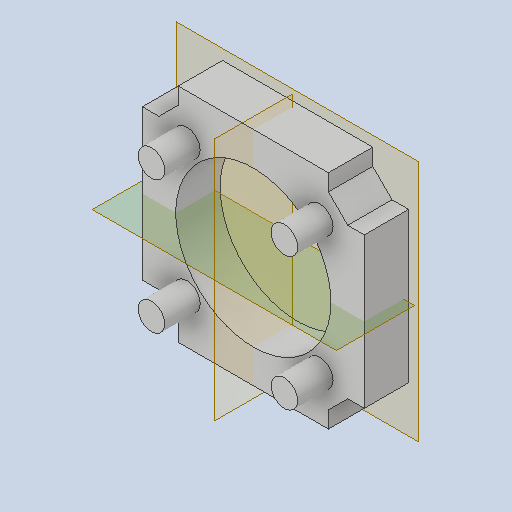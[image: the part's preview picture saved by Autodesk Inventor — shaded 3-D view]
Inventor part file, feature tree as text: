
AUTODESK INVENTOR PART (.ipt)
format: ipt  version: 2023 (Build 270158000, 158)  size: 226,816 bytes
history: native  units: mm
features: reference x19, other x5, plane x4, extrude x4, sketch x4, projected_geometry x1
ambient origin geometry x8: Origin, YZ Plane, XZ Plane, XY Plane, X Axis, Y Axis, Z Axis, Center Point
bodies: Solid1 (feature_tree)
feature tree (37):
  plane  "Work Plane1"
  extrude  "Extrusion1"  Depth=8.0mm TaperAngle=0.0deg
  sketch  "Sketch2"  dims[d18=53.8mm d19=45.0deg]
  plane  "Work Plane2"
  extrude  "Extrusion2"  TaperAngle=45.0deg  [1 undecoded]
  extrude  "Extrusion3"  Depth=45.0mm
  extrude  "Extrusion4"  Depth=10.0mm
  plane  "Arbeitsebene3"
  plane  "Arbeitsebene4"
  sketch  "Sketch1"  dims[d10=10.0mm d11=0.0mm d16=8.0mm d17=0.0mm]
  reference  "Reference1"
  reference  "Reference2"
  reference  "Reference3"
  reference  "Reference4"
  reference  "Reference5"
  reference  "Reference6"
  reference  "Reference7"
  reference  "Reference8"
  reference  "Reference9"
  sketch  "Sketch3"  dims[d20=53.8mm d21=45.0mm]
  reference  "Reference10"
  reference  "Reference11"
  reference  "Reference12"
  reference  "Reference13"
  reference  "Reference14"
  reference  "Reference15"
  reference  "Reference16"
  reference  "Reference17"
  reference  "Reference18"
  reference  "Reference19"
  sketch  "Sketch4"  dims[d22=45.0mm d23=0.1mm d24=0.1mm d25=0.1mm d26=0.1mm d27=0.1mm d28=3.0mm d29=0.0mm d1=6.0mm d31=6.0mm d32=6.0mm d33=6.0mm d34=0.15mm d35=10.0mm d36=0.0mm]
  projected_geometry  "Projected Loop1"
  other  "Assembly_Cube_v2_Thorlabs.iam"
  other  "10_Cube_Base:1"
  other  "CP02_M-Step:1"
  other  "00_Base_v0:1"
  other  "10_Cube_Lid:1"
note: 1 required parameter value undecoded (feature->parameter linkage not recoverable at this tier; creation-order binding heuristic only, values carry confidence <= 0.55)
